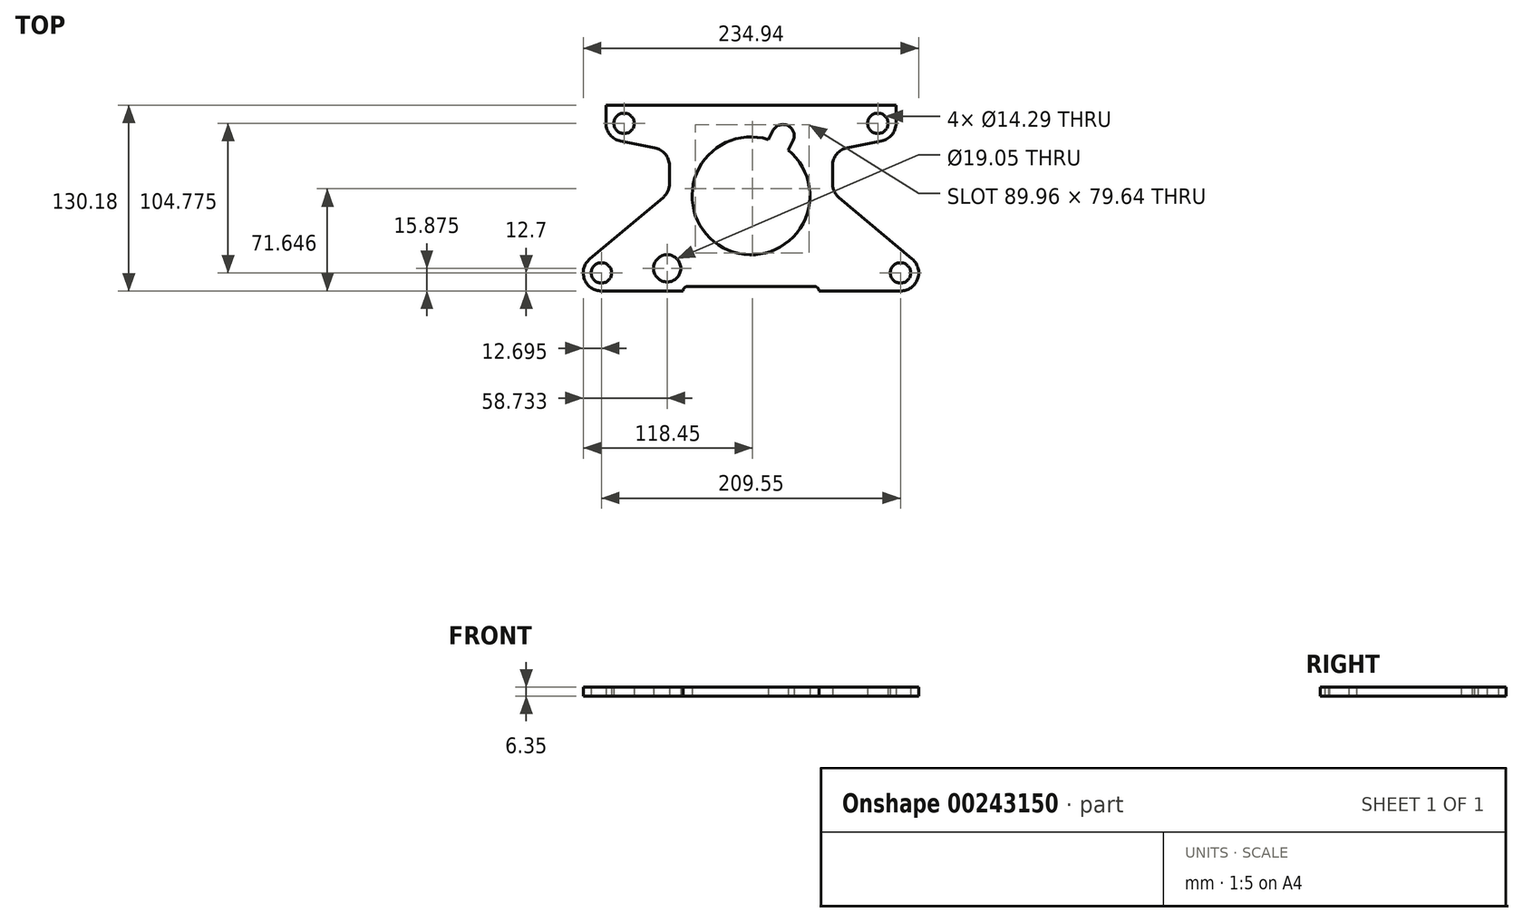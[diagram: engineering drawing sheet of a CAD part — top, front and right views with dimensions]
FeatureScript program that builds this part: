
annotation { "Feature Type Name" : "Feature", "Feature Type Description" : "" }
export const myFeature = defineFeature(function(context is Context, id is Id, definition is map)
    precondition{}
    {
        {
            var Q0;
            Q0=qCreatedBy(makeId("Top.planeOp"),FACE);
            var sketch = newSketch(context, id + "F0", { "sketchPlane" : qUnion([Q0])});
            skLineSegment(sketch, "E0.bottom", {"start": v(47.63, 0) * mm, "end": v(104.78, 0) * mm});
            skLineSegment(sketch, "E0.top", {"start": v(0, 130.18) * mm, "end": v(101.6, 130.18) * mm});
            skLineSegment(sketch, "E1", {"start": v(47.63, 0) * mm, "end": v(47.63, 0) * mm});
            skLineSegment(sketch, "E2", {"start": v(44.45, 3.18) * mm, "end": v(0, 3.17) * mm});
            skPoint(sketch, "E3.orphan", {"position": v(0, 0) * mm});
            skPoint(sketch, "E4.visualSharp", {"position": v(47.63, 3.18) * mm});
            skArc(sketch, "E4.filletArc", {"start": v(47.63, 0) * mm, "mid": v(46.7, 2.25) * mm, "end": v(44.45, 3.18) * mm});
            skArc(sketch, "E5", {"start": v(104.78, 0) * mm, "mid": v(116.71, 8.37) * mm, "end": v(112.92, 22.45) * mm});
            skCircle(sketch, "E6", {"center": v(104.78, 12.7) * mm, "radius": 7.14 * mm});
            skArc(sketch, "E7", {"start": v(0, 25.4) * mm, "mid": v(38.9, 52.87) * mm, "end": v(26.02, 98.71) * mm});
            skLineSegment(sketch, "E8", {"start": v(0, 130.18) * mm, "end": v(88.9, 130.18) * mm});
            skArc(sketch, "E9", {"start": v(91.32, 105) * mm, "mid": v(98.7, 109.4) * mm, "end": v(101.6, 117.47) * mm});
            skCircle(sketch, "E10", {"center": v(88.9, 117.47) * mm, "radius": 7.14 * mm});
            skLineSegment(sketch, "E11", {"start": v(57.15, 87.9) * mm, "end": v(57.15, 75.16) * mm});
            skLineSegment(sketch, "E12", {"start": v(91.32, 105) * mm, "end": v(67.43, 100.36) * mm});
            skLineSegment(sketch, "E13", {"start": v(57.15, 87.9) * mm, "end": v(57.15, 77.92) * mm});
            skPoint(sketch, "E14.orphan", {"position": v(57.15, 130.18) * mm});
            skLineSegment(sketch, "E15", {"start": v(112.96, 22.41) * mm, "end": v(61.69, 65.43) * mm});
            skLineSegment(sketch, "E16", {"start": v(88.9, 130.18) * mm, "end": v(101.6, 130.18) * mm});
            skLineSegment(sketch, "E17", {"start": v(101.6, 130.18) * mm, "end": v(101.6, 117.47) * mm});
            skPoint(sketch, "E18.orphan", {"position": v(114.3, 130.18) * mm});
            skPoint(sketch, "E19.visualSharp", {"position": v(57.15, 98.37) * mm});
            skArc(sketch, "E19.filletArc", {"start": v(67.43, 100.36) * mm, "mid": v(60.05, 95.97) * mm, "end": v(57.15, 87.9) * mm});
            skPoint(sketch, "E20.newPointB", {"position": v(57.15, 0) * mm});
            skArc(sketch, "E20.filletArc", {"start": v(57.15, 75.16) * mm, "mid": v(58.34, 69.8) * mm, "end": v(61.69, 65.43) * mm});
            skArc(sketch, "E21.MirrorCS", {"start": v(-47.63, 0) * mm, "mid": v(-46.7, 2.25) * mm, "end": v(-44.45, 3.18) * mm});
            skArc(sketch, "E22.MirrorCS", {"start": v(-57.15, 75.16) * mm, "mid": v(-58.34, 69.8) * mm, "end": v(-61.69, 65.43) * mm});
            skLineSegment(sketch, "E23.MirrorCS", {"start": v(-57.15, 87.9) * mm, "end": v(-57.15, 75.16) * mm});
            skLineSegment(sketch, "E24.MirrorCS", {"start": v(-88.9, 130.18) * mm, "end": v(-101.6, 130.18) * mm});
            skLineSegment(sketch, "E25.MirrorCS", {"start": v(-57.15, 87.9) * mm, "end": v(-57.15, 77.92) * mm});
            skLineSegment(sketch, "E26.MirrorCS", {"start": v(-112.96, 22.41) * mm, "end": v(-61.69, 65.43) * mm});
            skLineSegment(sketch, "E27.MirrorCS", {"start": v(0, 130.18) * mm, "end": v(-101.6, 130.18) * mm});
            skLineSegment(sketch, "E28.MirrorCS", {"start": v(-47.63, 0) * mm, "end": v(-104.78, 0) * mm});
            skLineSegment(sketch, "E29.MirrorCS", {"start": v(-91.32, 105) * mm, "end": v(-67.43, 100.36) * mm});
            skArc(sketch, "E30.MirrorCS", {"start": v(-67.43, 100.36) * mm, "mid": v(-60.05, 95.97) * mm, "end": v(-57.15, 87.9) * mm});
            skArc(sketch, "E31.MirrorCS", {"start": v(-91.32, 105) * mm, "mid": v(-98.7, 109.4) * mm, "end": v(-101.6, 117.47) * mm});
            skCircle(sketch, "E32.MirrorC", {"center": v(-88.9, 117.47) * mm, "radius": 7.14 * mm});
            skPoint(sketch, "E33.MirrorP", {"position": v(-114.3, 130.18) * mm});
            skPoint(sketch, "E34.MirrorP", {"position": v(-47.63, 3.18) * mm});
            skLineSegment(sketch, "E35.MirrorCS", {"start": v(-101.6, 130.18) * mm, "end": v(-101.6, 117.47) * mm});
            skArc(sketch, "E36.MirrorCS", {"start": v(0, 25.4) * mm, "mid": v(-41.28, 66.67) * mm, "end": v(0, 107.95) * mm});
            skLineSegment(sketch, "E37.MirrorCS", {"start": v(0, 130.18) * mm, "end": v(-88.9, 130.18) * mm});
            skCircle(sketch, "E38.MirrorC", {"center": v(-104.78, 12.7) * mm, "radius": 7.14 * mm});
            skArc(sketch, "E39.MirrorCS", {"start": v(-104.78, 0) * mm, "mid": v(-116.71, 8.37) * mm, "end": v(-112.92, 22.45) * mm});
            skLineSegment(sketch, "E40.MirrorCS", {"start": v(-44.45, 3.17) * mm, "end": v(0, 3.17) * mm});
            skPoint(sketch, "E41.MirrorP", {"position": v(-57.15, 130.18) * mm});
            skPoint(sketch, "E42.MirrorP", {"position": v(-57.15, 98.37) * mm});
            skPoint(sketch, "E43.MirrorP", {"position": v(-57.15, 0) * mm});
            skLineSegment(sketch, "E44", {"start": v(-104.78, 0) * mm, "end": v(-57.15, 0) * mm});
            skCircle(sketch, "E45", {"center": v(-58.74, 15.87) * mm, "radius": 9.53 * mm});
            skArc(sketch, "E46", {"start": v(29.37, 105) * mm, "mid": v(26.09, 115.73) * mm, "end": v(15.35, 112.45) * mm});
            skArc(sketch, "E47.trimOffspring", {"start": v(12, 106.16) * mm, "mid": v(6.07, 107.5) * mm, "end": v(0, 107.95) * mm});
            skLineSegment(sketch, "E48", {"start": v(29.37, 105) * mm, "end": v(26.02, 98.71) * mm});
            skLineSegment(sketch, "E49", {"start": v(26.02, 98.71) * mm, "end": v(29.37, 105) * mm});
            skLineSegment(sketch, "E50", {"start": v(15.35, 112.45) * mm, "end": v(12, 106.16) * mm});
            skLineSegment(sketch, "E51", {"start": v(0, 107.95) * mm, "end": v(0, 66.68) * mm});
            skLineSegment(sketch, "E52", {"start": v(22.36, 108.73) * mm, "end": v(0, 66.68) * mm});
            skSolve(sketch);
        }
        {
            var Q0;
            Q0 = qSketchRegion(id + "F0", true);
            extrude(context, id + "F1", {"entities" : qUnion([Q0]), "depth" : 6.35 * mm});
        }
    });
